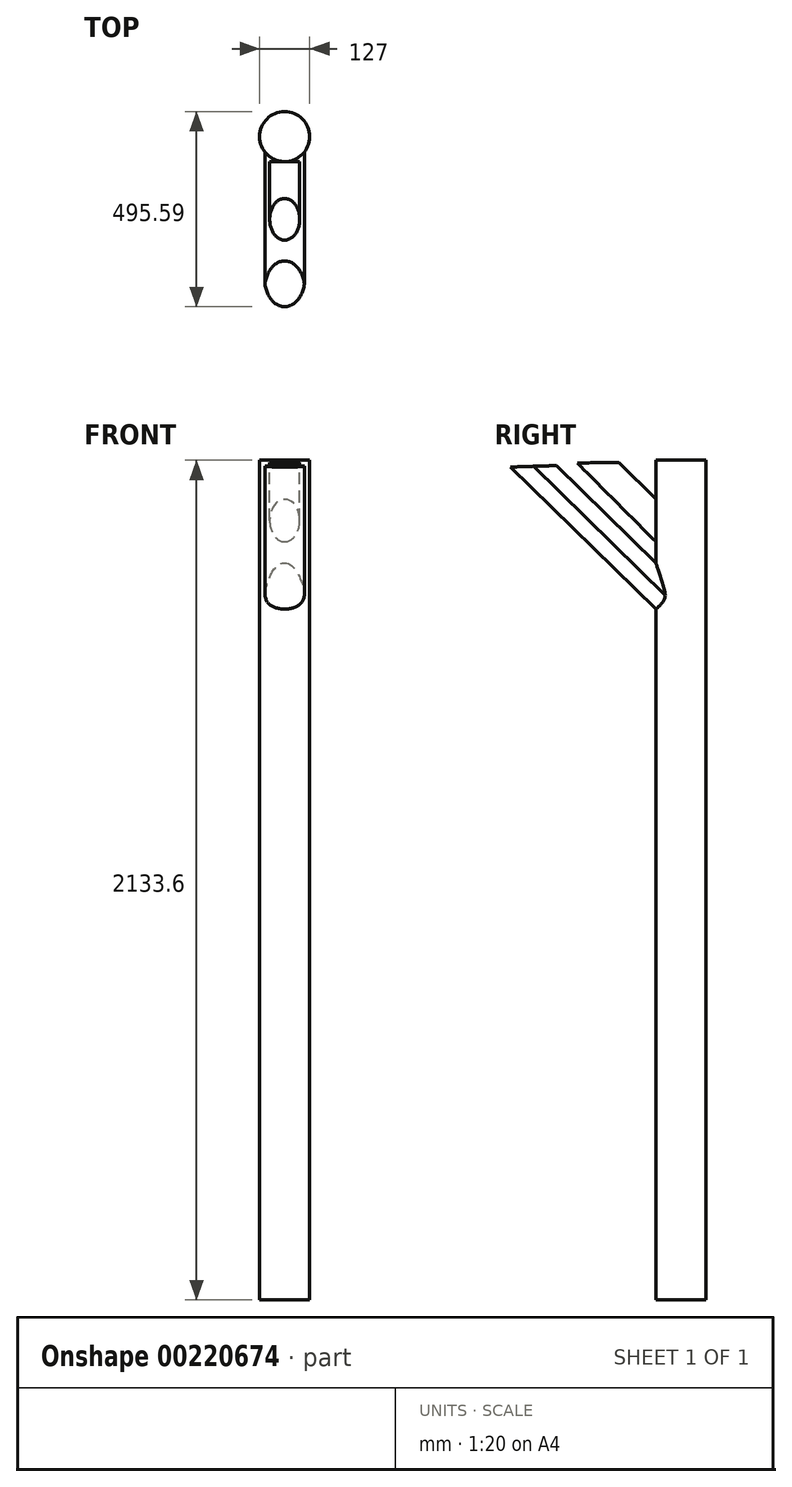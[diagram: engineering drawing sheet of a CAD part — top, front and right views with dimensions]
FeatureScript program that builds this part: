
annotation { "Feature Type Name" : "Feature", "Feature Type Description" : "" }
export const myFeature = defineFeature(function(context is Context, id is Id, definition is map)
    precondition{}
    {
        {
            var Q0;
            Q0=qCreatedBy(makeId("Right.planeOp"),FACE);
            var sketch = newSketch(context, id + "F0", { "sketchPlane" : qUnion([Q0])});
            skLineSegment(sketch, "E0.bottom", {"start": v(-127, 0) * mm, "end": v(0, 0) * mm});
            skLineSegment(sketch, "E0.top", {"start": v(-127, 2133.6) * mm, "end": v(0, 2133.6) * mm});
            skLineSegment(sketch, "E0.left", {"start": v(0, 0) * mm, "end": v(0, 2133.6) * mm});
            skLineSegment(sketch, "E0.right", {"start": v(-127, 0) * mm, "end": v(-127, 2133.6) * mm});
            skLineSegment(sketch, "E1", {"start": v(-495.59, 2116.26) * mm, "end": v(-127, 1755.46) * mm});
            skLineSegment(sketch, "E2.0", {"start": v(-379.51, 2119.93) * mm, "end": v(-127, 1872.75) * mm});
            skLineSegment(sketch, "E3", {"start": v(-127, 1926.4) * mm, "end": v(-326.4, 2126.37) * mm});
            skLineSegment(sketch, "E4.0", {"start": v(-127, 2034.32) * mm, "end": v(-220.6, 2128.19) * mm});
            skLineSegment(sketch, "E5", {"start": v(-220.6, 2128.19) * mm, "end": v(-326.4, 2126.37) * mm});
            skLineSegment(sketch, "E6", {"start": v(-379.51, 2119.93) * mm, "end": v(-495.59, 2116.26) * mm});
            skSolve(sketch);
        }
        {
            var Q0;
            {var subQ1=sQuery(id+"F0.wireOp",EDGE,"E0.bottom");Q0=makeQuery(id+"F0.imprint","IMPRINT",FACE,{"disambiguationData":[TD([[makeQuery(id+"F0.imprint","IMPRINT",EDGE,{"derivedFrom":subQ1}),1.0]])]});}
            extrude(context, id + "F1", {"entities" : qUnion([Q0]), "endBound" : BoundingType.SYMMETRIC, "depth" : 127 * mm});
        }
        {
            var Q0;
            {var subQ0=sQuery(id+"F0.wireOp",EDGE,"E3");Q0=makeQuery(id+"F0.imprint","IMPRINT",FACE,{"disambiguationData":[TD([[makeQuery(id+"F0.imprint","IMPRINT",EDGE,{"derivedFrom":subQ0}),-1.0]])]});}
            extrude(context, id + "F2", {"entities" : qUnion([Q0]), "endBound" : BoundingType.SYMMETRIC, "depth" : 76.2 * mm});
        }
        {
            var Q0;
            {var subQ0=sQuery(id+"F0.wireOp",EDGE,"E1");Q0=makeQuery(id+"F0.imprint","IMPRINT",FACE,{"disambiguationData":[TD([[makeQuery(id+"F0.imprint","IMPRINT",EDGE,{"derivedFrom":subQ0}),1.0]])]});}
            extrude(context, id + "F3", {"entities" : qUnion([Q0]), "operationType" : NewBodyOperationType.ADD, "endBound" : BoundingType.SYMMETRIC, "depth" : 101.6 * mm});
        }
        {
            var Q0;
            Q0=makeQuery(id+"F1.opExtrude","CAP_EDGE",EDGE,{"disambiguationData":[OSD([sQuery(id+"F0.wireOp",EDGE,"E0.left")])],"isStart":true});
            var Q1;
            Q1=makeQuery(id+"F1.opExtrude","CAP_EDGE",EDGE,{"disambiguationData":[OSD([sQuery(id+"F0.wireOp",EDGE,"E0.right")])],"isStart":true});
            var Q2;
            Q2=makeQuery(id+"F1.opExtrude","CAP_EDGE",EDGE,{"disambiguationData":[OSD([sQuery(id+"F0.wireOp",EDGE,"E0.right")])],"isStart":false});
            var Q3;
            Q3=makeQuery(id+"F1.opExtrude","CAP_EDGE",EDGE,{"disambiguationData":[OSD([sQuery(id+"F0.wireOp",EDGE,"E0.left")])],"isStart":false});
            fillet(context, id + "F4", {"entities" : qUnion([Q0, Q1, Q2, Q3]), "radius" : 63.5 * mm, "tangentPropagation" : true, "allowEdgeOverflow" : false});
        }
        {
            var Q0;
            Q0=makeQuery(id+"F2.opExtrude","CAP_EDGE",EDGE,{"disambiguationData":[OSD([sQuery(id+"F0.wireOp",EDGE,"E3")])],"isStart":true});
            var Q1;
            Q1=makeQuery(id+"F2.opExtrude","CAP_EDGE",EDGE,{"disambiguationData":[OSD([sQuery(id+"F0.wireOp",EDGE,"E4.0")])],"isStart":true});
            var Q2;
            Q2=makeQuery(id+"F2.opExtrude","CAP_EDGE",EDGE,{"disambiguationData":[OSD([sQuery(id+"F0.wireOp",EDGE,"E4.0")])],"isStart":false});
            var Q3;
            Q3=makeQuery(id+"F2.opExtrude","CAP_EDGE",EDGE,{"disambiguationData":[OSD([sQuery(id+"F0.wireOp",EDGE,"E3")])],"isStart":false});
            fillet(context, id + "F5", {"entities" : qUnion([Q0, Q1, Q2, Q3]), "radius" : 38.1 * mm, "tangentPropagation" : true, "allowEdgeOverflow" : false});
        }
        {
            var Q0;
            Q0=makeQuery(id+"F3.opExtrude","CAP_EDGE",EDGE,{"disambiguationData":[OSD([sQuery(id+"F0.wireOp",EDGE,"E1")])],"isStart":true});
            var Q1;
            Q1=makeQuery(id+"F3.opExtrude","CAP_EDGE",EDGE,{"disambiguationData":[OSD([sQuery(id+"F0.wireOp",EDGE,"E2.0")])],"isStart":true});
            var Q2;
            Q2=makeQuery(id+"F3.opExtrude","CAP_EDGE",EDGE,{"disambiguationData":[OSD([sQuery(id+"F0.wireOp",EDGE,"E2.0")])],"isStart":false});
            var Q3;
            Q3=makeQuery(id+"F3.opExtrude","CAP_EDGE",EDGE,{"disambiguationData":[OSD([sQuery(id+"F0.wireOp",EDGE,"E1")])],"isStart":false});
            fillet(context, id + "F6", {"entities" : qUnion([Q0, Q1, Q2, Q3]), "radius" : 50.55 * mm, "tangentPropagation" : true, "allowEdgeOverflow" : false});
        }
    });
